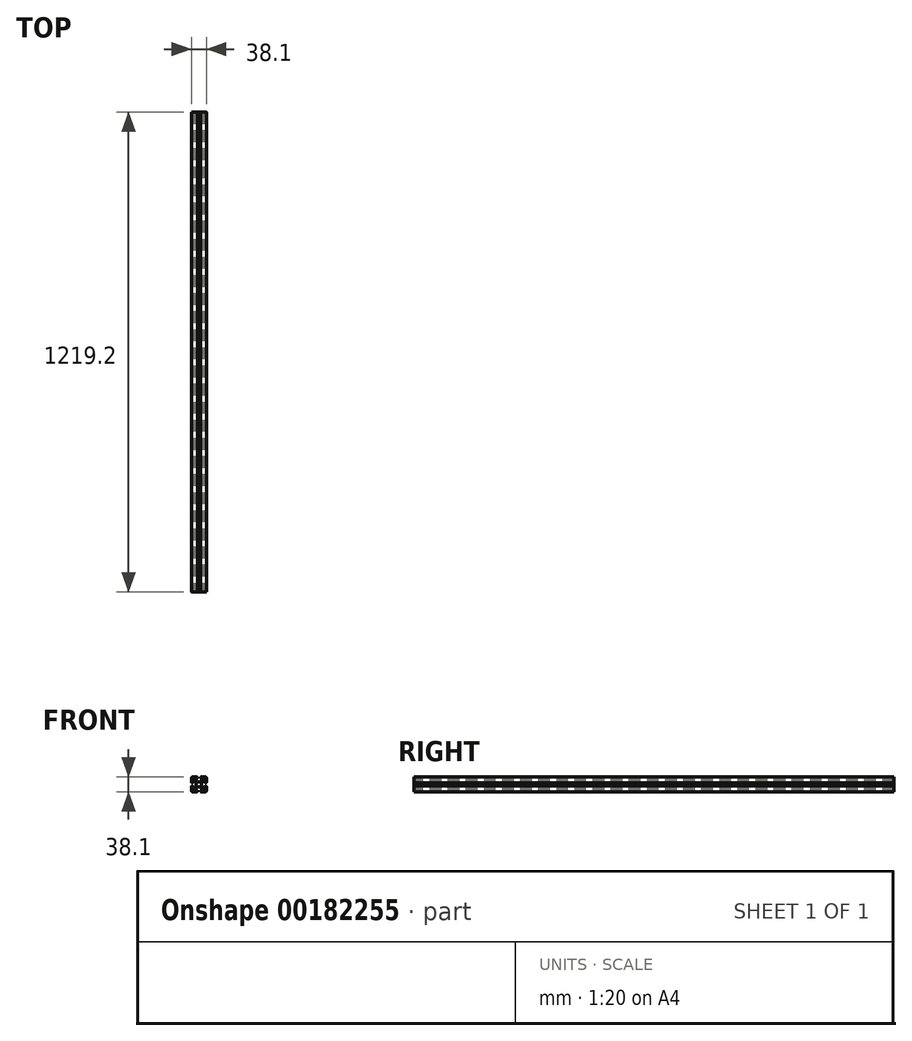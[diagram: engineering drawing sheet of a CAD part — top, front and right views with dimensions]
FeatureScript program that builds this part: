
annotation { "Feature Type Name" : "Feature", "Feature Type Description" : "" }
export const myFeature = defineFeature(function(context is Context, id is Id, definition is map)
    precondition{}
    {
        {
            var Q0;
            Q0=qCreatedBy(makeId("Front.planeOp"),FACE);
            var sketch = newSketch(context, id + "F0", { "sketchPlane" : qUnion([Q0])});
            skLineSegment(sketch, "E0", {"start": v(-16.03, 19.4) * mm, "end": v(-5.8, 19.4) * mm});
            skLineSegment(sketch, "E1.0", {"start": v(-19.2, 16.23) * mm, "end": v(-19.2, 5.99) * mm});
            skArc(sketch, "E2.0", {"start": v(-16.03, 19.4) * mm, "mid": v(-18.28, 18.47) * mm, "end": v(-19.2, 16.23) * mm});
            skArc(sketch, "E3.0", {"start": v(-19.2, 5.99) * mm, "mid": v(-18.75, 4.88) * mm, "end": v(-17.63, 4.41) * mm});
            skLineSegment(sketch, "E4.0", {"start": v(-17.63, 4.41) * mm, "end": v(-16.72, 4.41) * mm});
            skArc(sketch, "E5.0", {"start": v(-16.72, 4.41) * mm, "mid": v(-15.6, 4.88) * mm, "end": v(-15.15, 5.99) * mm});
            skLineSegment(sketch, "E6.0", {"start": v(-15.15, 5.99) * mm, "end": v(-15.15, 9.75) * mm});
            skArc(sketch, "E7.0", {"start": v(-15.15, 9.75) * mm, "mid": v(-14.89, 10.38) * mm, "end": v(-14.26, 10.64) * mm});
            skLineSegment(sketch, "E8.0", {"start": v(-14.26, 10.64) * mm, "end": v(-13.69, 10.64) * mm});
            skArc(sketch, "E9.0", {"start": v(-13.69, 10.64) * mm, "mid": v(-13.35, 10.57) * mm, "end": v(-13.06, 10.38) * mm});
            skLineSegment(sketch, "E10.0", {"start": v(-13.06, 10.38) * mm, "end": v(-8.42, 5.74) * mm});
            skArc(sketch, "E11.0", {"start": v(-8.42, 5.74) * mm, "mid": v(-7.4, 4.2) * mm, "end": v(-7.03, 2.38) * mm});
            skLineSegment(sketch, "E12.0", {"start": v(-7.03, 2.38) * mm, "end": v(-7.03, -1.68) * mm});
            skArc(sketch, "E13.0", {"start": v(-7.03, -1.68) * mm, "mid": v(-7.4, -3.5) * mm, "end": v(-8.42, -5.04) * mm});
            skLineSegment(sketch, "E14.0", {"start": v(-8.42, -5.04) * mm, "end": v(-13.06, -9.68) * mm});
            skArc(sketch, "E15.0", {"start": v(-13.06, -9.68) * mm, "mid": v(-13.35, -9.87) * mm, "end": v(-13.69, -9.94) * mm});
            skLineSegment(sketch, "E16.0", {"start": v(-13.69, -9.94) * mm, "end": v(-14.26, -9.94) * mm});
            skArc(sketch, "E17.0", {"start": v(-14.26, -9.94) * mm, "mid": v(-14.89, -9.68) * mm, "end": v(-15.15, -9.05) * mm});
            skLineSegment(sketch, "E18.0", {"start": v(-15.15, -9.05) * mm, "end": v(-15.15, -5.29) * mm});
            skArc(sketch, "E19.0", {"start": v(-15.15, -5.29) * mm, "mid": v(-15.6, -4.17) * mm, "end": v(-16.72, -3.71) * mm});
            skLineSegment(sketch, "E20.0", {"start": v(-16.72, -3.71) * mm, "end": v(-17.63, -3.71) * mm});
            skArc(sketch, "E21.0", {"start": v(-17.63, -3.71) * mm, "mid": v(-18.75, -4.17) * mm, "end": v(-19.2, -5.29) * mm});
            skLineSegment(sketch, "E22.0", {"start": v(-19.2, -5.29) * mm, "end": v(-19.2, -15.52) * mm});
            skArc(sketch, "E23.0", {"start": v(-19.2, -15.52) * mm, "mid": v(-18.28, -17.77) * mm, "end": v(-16.03, -18.7) * mm});
            skLineSegment(sketch, "E24.0", {"start": v(-16.03, -18.7) * mm, "end": v(-5.8, -18.7) * mm});
            skArc(sketch, "E25.0", {"start": v(-5.8, -18.7) * mm, "mid": v(-4.68, -18.24) * mm, "end": v(-4.22, -17.12) * mm});
            skLineSegment(sketch, "E26.0", {"start": v(-4.22, -17.12) * mm, "end": v(-4.22, -16.2) * mm});
            skArc(sketch, "E27.0", {"start": v(-4.22, -16.2) * mm, "mid": v(-4.68, -15.1) * mm, "end": v(-5.8, -14.64) * mm});
            skLineSegment(sketch, "E28.0", {"start": v(-5.8, -14.64) * mm, "end": v(-9.56, -14.64) * mm});
            skArc(sketch, "E29.0", {"start": v(-9.56, -14.64) * mm, "mid": v(-10.19, -14.37) * mm, "end": v(-10.45, -13.75) * mm});
            skLineSegment(sketch, "E30.0", {"start": v(-10.45, -13.75) * mm, "end": v(-10.45, -13.18) * mm});
            skArc(sketch, "E31.0", {"start": v(-10.45, -13.18) * mm, "mid": v(-10.38, -12.84) * mm, "end": v(-10.19, -12.55) * mm});
            skLineSegment(sketch, "E32.0", {"start": v(-10.19, -12.55) * mm, "end": v(-5.55, -7.91) * mm});
            skArc(sketch, "E33.0", {"start": v(-5.55, -7.91) * mm, "mid": v(-4, -6.88) * mm, "end": v(-2.19, -6.52) * mm});
            skLineSegment(sketch, "E34.0", {"start": v(-2.19, -6.52) * mm, "end": v(1.87, -6.52) * mm});
            skArc(sketch, "E35.0", {"start": v(1.87, -6.52) * mm, "mid": v(3.69, -6.88) * mm, "end": v(5.23, -7.91) * mm});
            skLineSegment(sketch, "E36.0", {"start": v(5.23, -7.91) * mm, "end": v(9.87, -12.55) * mm});
            skArc(sketch, "E37.0", {"start": v(9.87, -12.55) * mm, "mid": v(10.06, -12.84) * mm, "end": v(10.13, -13.18) * mm});
            skPoint(sketch, "E38.0", {"position": v(10.13, -13.75) * mm});
            skArc(sketch, "E39.0", {"start": v(10.13, -13.75) * mm, "mid": v(9.87, -14.37) * mm, "end": v(9.24, -14.64) * mm});
            skLineSegment(sketch, "E40.0", {"start": v(9.24, -14.64) * mm, "end": v(5.48, -14.64) * mm});
            skArc(sketch, "E41.0", {"start": v(5.48, -14.64) * mm, "mid": v(4.37, -15.1) * mm, "end": v(3.9, -16.2) * mm});
            skPoint(sketch, "E42.0", {"position": v(3.9, -17.12) * mm});
            skLineSegment(sketch, "E43.0", {"start": v(3.9, -16.2) * mm, "end": v(3.9, -17.12) * mm});
            skArc(sketch, "E44.0", {"start": v(3.9, -17.12) * mm, "mid": v(4.37, -18.24) * mm, "end": v(5.48, -18.7) * mm});
            skLineSegment(sketch, "E45.0", {"start": v(5.48, -18.7) * mm, "end": v(15.72, -18.7) * mm});
            skArc(sketch, "E46.0", {"start": v(15.72, -18.7) * mm, "mid": v(17.96, -17.77) * mm, "end": v(18.9, -15.52) * mm});
            skLineSegment(sketch, "E47.0", {"start": v(18.9, -15.52) * mm, "end": v(18.9, -5.29) * mm});
            skArc(sketch, "E48.0", {"start": v(18.9, -5.29) * mm, "mid": v(18.43, -4.17) * mm, "end": v(17.32, -3.71) * mm});
            skLineSegment(sketch, "E49.0", {"start": v(17.32, -3.71) * mm, "end": v(16.4, -3.71) * mm});
            skArc(sketch, "E50.0", {"start": v(16.4, -3.71) * mm, "mid": v(15.29, -4.17) * mm, "end": v(14.83, -5.29) * mm});
            skLineSegment(sketch, "E51.0", {"start": v(14.83, -5.29) * mm, "end": v(14.83, -9.05) * mm});
            skArc(sketch, "E52.0", {"start": v(14.83, -9.05) * mm, "mid": v(14.57, -9.68) * mm, "end": v(13.94, -9.94) * mm});
            skLineSegment(sketch, "E53.0", {"start": v(13.94, -9.94) * mm, "end": v(13.37, -9.94) * mm});
            skArc(sketch, "E54.0", {"start": v(13.37, -9.94) * mm, "mid": v(13.03, -9.87) * mm, "end": v(12.74, -9.68) * mm});
            skLineSegment(sketch, "E55.0", {"start": v(12.74, -9.68) * mm, "end": v(8.1, -5.04) * mm});
            skArc(sketch, "E56.0", {"start": v(8.1, -5.04) * mm, "mid": v(7.07, -3.5) * mm, "end": v(6.71, -1.68) * mm});
            skLineSegment(sketch, "E57.0", {"start": v(6.71, -1.68) * mm, "end": v(6.71, 2.38) * mm});
            skArc(sketch, "E58.0", {"start": v(6.71, 2.38) * mm, "mid": v(7.07, 4.2) * mm, "end": v(8.1, 5.74) * mm});
            skLineSegment(sketch, "E59.0", {"start": v(8.1, 5.74) * mm, "end": v(12.74, 10.38) * mm});
            skArc(sketch, "E60.0", {"start": v(12.74, 10.38) * mm, "mid": v(13.03, 10.57) * mm, "end": v(13.37, 10.64) * mm});
            skLineSegment(sketch, "E61.0", {"start": v(13.37, 10.64) * mm, "end": v(13.94, 10.64) * mm});
            skArc(sketch, "E62.0", {"start": v(13.94, 10.64) * mm, "mid": v(14.57, 10.38) * mm, "end": v(14.83, 9.75) * mm});
            skLineSegment(sketch, "E63.0", {"start": v(14.83, 9.75) * mm, "end": v(14.83, 5.99) * mm});
            skArc(sketch, "E64.0", {"start": v(14.83, 5.99) * mm, "mid": v(15.29, 4.88) * mm, "end": v(16.4, 4.41) * mm});
            skLineSegment(sketch, "E65.0", {"start": v(16.4, 4.41) * mm, "end": v(17.32, 4.41) * mm});
            skArc(sketch, "E66.0", {"start": v(17.32, 4.41) * mm, "mid": v(18.43, 4.88) * mm, "end": v(18.9, 5.99) * mm});
            skLineSegment(sketch, "E67.0", {"start": v(18.9, 5.99) * mm, "end": v(18.9, 16.23) * mm});
            skArc(sketch, "E68.0", {"start": v(18.9, 16.23) * mm, "mid": v(17.96, 18.47) * mm, "end": v(15.72, 19.4) * mm});
            skLineSegment(sketch, "E69.0", {"start": v(15.72, 19.4) * mm, "end": v(5.48, 19.4) * mm});
            skArc(sketch, "E70.0", {"start": v(5.48, 19.4) * mm, "mid": v(4.37, 18.94) * mm, "end": v(3.9, 17.83) * mm});
            skLineSegment(sketch, "E71.0", {"start": v(3.9, 17.83) * mm, "end": v(3.9, 16.91) * mm});
            skArc(sketch, "E72.0", {"start": v(3.9, 16.91) * mm, "mid": v(4.37, 15.8) * mm, "end": v(5.48, 15.34) * mm});
            skLineSegment(sketch, "E73.0", {"start": v(5.48, 15.34) * mm, "end": v(9.24, 15.34) * mm});
            skArc(sketch, "E74.0", {"start": v(9.24, 15.34) * mm, "mid": v(9.87, 15.08) * mm, "end": v(10.13, 14.45) * mm});
            skLineSegment(sketch, "E75.0", {"start": v(10.13, 14.45) * mm, "end": v(10.13, 13.88) * mm});
            skArc(sketch, "E76.0", {"start": v(10.13, 13.88) * mm, "mid": v(10.06, 13.54) * mm, "end": v(9.87, 13.25) * mm});
            skLineSegment(sketch, "E77.0", {"start": v(9.87, 13.25) * mm, "end": v(5.23, 8.61) * mm});
            skArc(sketch, "E78.0", {"start": v(-4.22, 17.83) * mm, "mid": v(-4.68, 18.94) * mm, "end": v(-5.8, 19.4) * mm});
            skLineSegment(sketch, "E79.0", {"start": v(-4.22, 16.91) * mm, "end": v(-4.22, 17.83) * mm});
            skArc(sketch, "E80.0", {"start": v(-5.8, 15.34) * mm, "mid": v(-4.68, 15.8) * mm, "end": v(-4.22, 16.91) * mm});
            skLineSegment(sketch, "E81.0", {"start": v(-9.56, 15.34) * mm, "end": v(-5.8, 15.34) * mm});
            skArc(sketch, "E82.0", {"start": v(-10.45, 14.45) * mm, "mid": v(-10.19, 15.08) * mm, "end": v(-9.56, 15.34) * mm});
            skLineSegment(sketch, "E83.0", {"start": v(-10.45, 13.88) * mm, "end": v(-10.45, 14.45) * mm});
            skArc(sketch, "E84.0", {"start": v(-10.19, 13.25) * mm, "mid": v(-10.38, 13.54) * mm, "end": v(-10.45, 13.88) * mm});
            skLineSegment(sketch, "E85.0", {"start": v(-5.55, 8.61) * mm, "end": v(-10.19, 13.25) * mm});
            skArc(sketch, "E86.0", {"start": v(-2.19, 7.22) * mm, "mid": v(-4, 7.58) * mm, "end": v(-5.55, 8.61) * mm});
            skLineSegment(sketch, "E87.0", {"start": v(1.87, 7.22) * mm, "end": v(-2.19, 7.22) * mm});
            skArc(sketch, "E88.0", {"start": v(5.23, 8.61) * mm, "mid": v(3.69, 7.58) * mm, "end": v(1.87, 7.22) * mm});
            skLineSegment(sketch, "E89.0", {"start": v(10.13, -13.18) * mm, "end": v(10.13, -13.75) * mm});
            skSolve(sketch);
        }
        {
            var Q0;
            Q0=qSketchRegion(id+"F0",true);
            extrude(context, id + "F1", {"entities" : qUnion([Q0]), "oppositeDirection" : true, "depth" : 1219.2 * mm});
        }
    });
